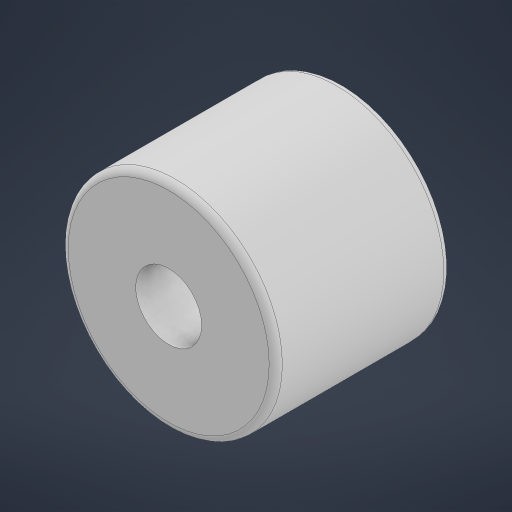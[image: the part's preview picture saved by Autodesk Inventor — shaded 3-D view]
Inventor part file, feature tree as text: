
AUTODESK INVENTOR PART (.ipt)
format: ipt  version: 2023 (Build 270158000, 158)  size: 185,344 bytes
history: native  units: mm
features: extrude x1, fillet x1, sketch x1
ambient origin geometry x8: Origin, YZ Plane, XZ Plane, XY Plane, X Axis, Y Axis, Z Axis, Center Point
bodies: Solid1 (feature_tree)
feature tree (3):
  extrude  "Extrusion1"  Depth=2.0mm
  fillet  "Fillet1"  Radius=53.0mm
  sketch  "Sketch1"  dims[d0=65.0mm d1=20.0mm d2=53.0mm d3=0.0mm d4=2.0mm]
